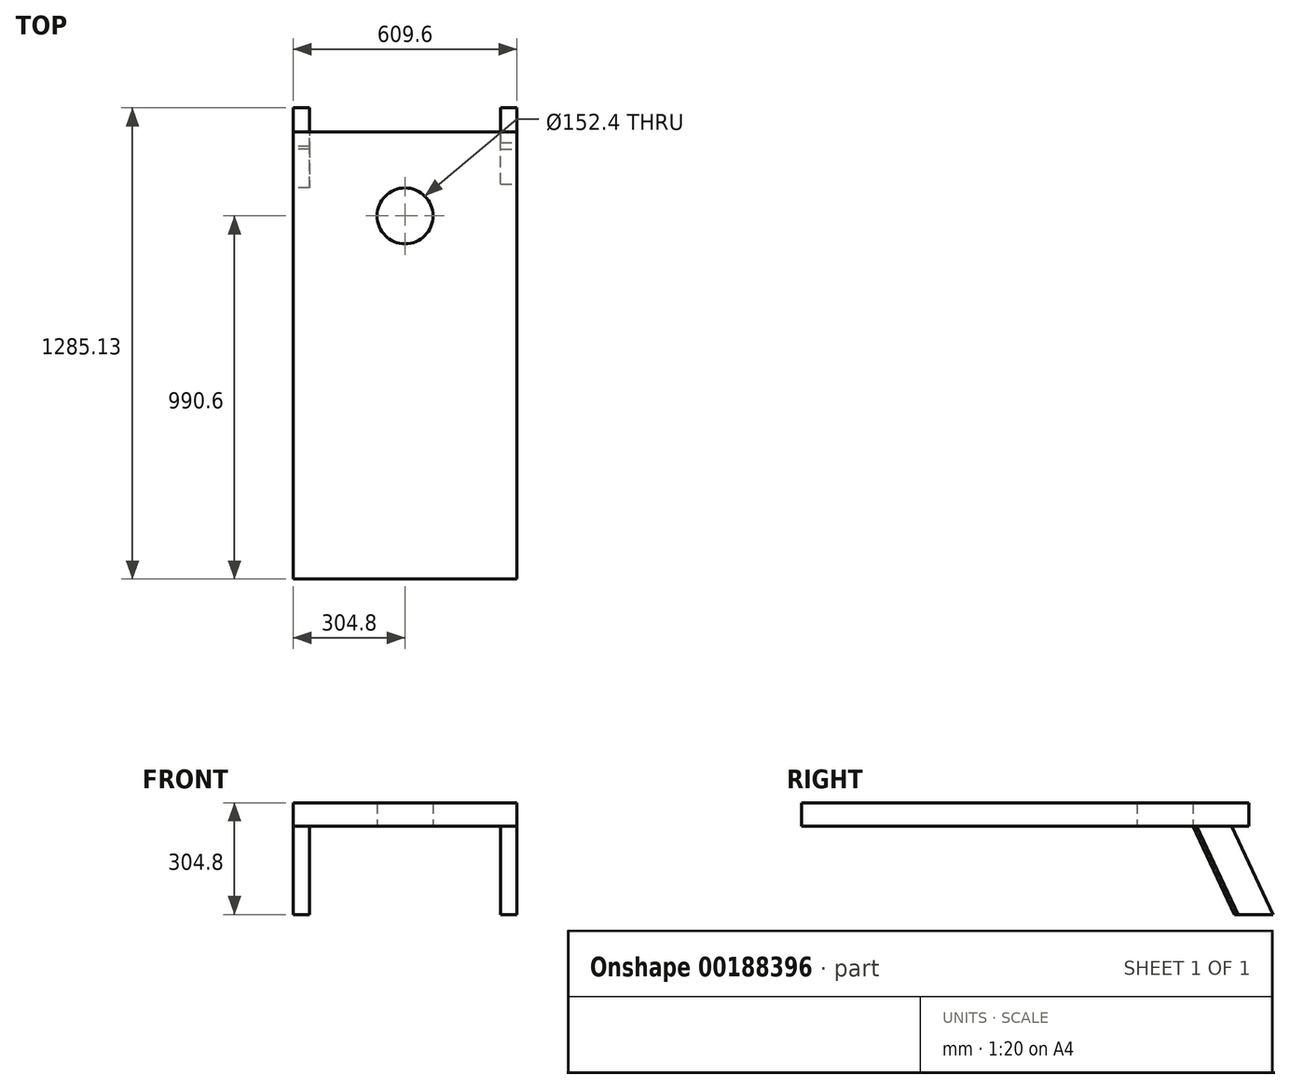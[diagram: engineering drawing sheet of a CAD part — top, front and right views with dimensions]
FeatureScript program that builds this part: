
annotation { "Feature Type Name" : "Feature", "Feature Type Description" : "" }
export const myFeature = defineFeature(function(context is Context, id is Id, definition is map)
    precondition{}
    {
        {
            var Q0;
            Q0=qCreatedBy(makeId("Top.planeOp"),FACE);
            var sketch = newSketch(context, id + "F0", { "sketchPlane" : qUnion([Q0])});
            skLineSegment(sketch, "E0.bottom", {"start": v(0, 0) * mm, "end": v(609.6, 0) * mm});
            skLineSegment(sketch, "E0.top", {"start": v(0, 1219.2) * mm, "end": v(609.6, 1219.2) * mm});
            skLineSegment(sketch, "E0.left", {"start": v(0, 0) * mm, "end": v(0, 1219.2) * mm});
            skLineSegment(sketch, "E0.right", {"start": v(609.6, 0) * mm, "end": v(609.6, 1219.2) * mm});
            skCircle(sketch, "E1", {"center": v(304.8, 990.6) * mm, "radius": 76.2 * mm});
            skLineSegment(sketch, "E2", {"start": v(0, 990.6) * mm, "end": v(609.6, 990.6) * mm});
            skLineSegment(sketch, "E3", {"start": v(304.8, 1219.2) * mm, "end": v(304.8, 0) * mm});
            skSolve(sketch);
        }
        {
            var Q0;
            {var subQ1=sQuery(id+"F0.wireOp",EDGE,"E0.left");var subQ5=sQuery(id+"F0.wireOp",EDGE,"E0.top");var subQ6=makeQuery(id+"F0.imprint","INTERSECT",VERTEX,{"derivedFrom":[subQ5,subQ1]});Q0=makeQuery(id+"F0.imprint","IMPRINT",FACE,{"disambiguationData":[TD([[makeQuery(id+"F0.imprint","IMPRINT",EDGE,{"disambiguationData":[TD([[subQ6,-1.0]])],"derivedFrom":subQ5}),-1.0]])]});}
            var Q1;
            {var subQ1=sQuery(id+"F0.wireOp",EDGE,"E0.right");var subQ7=sQuery(id+"F0.wireOp",EDGE,"E0.top");var subQ8=makeQuery(id+"F0.imprint","INTERSECT",VERTEX,{"derivedFrom":[subQ7,subQ1]});Q1=makeQuery(id+"F0.imprint","IMPRINT",FACE,{"disambiguationData":[TD([[makeQuery(id+"F0.imprint","IMPRINT",EDGE,{"disambiguationData":[TD([[subQ8,1.0]])],"derivedFrom":subQ7}),-1.0]])]});}
            var Q2;
            {var subQ1=sQuery(id+"F0.wireOp",EDGE,"E0.right");var subQ7=sQuery(id+"F0.wireOp",EDGE,"E0.bottom");var subQ8=makeQuery(id+"F0.imprint","INTERSECT",VERTEX,{"derivedFrom":[subQ7,subQ1]});Q2=makeQuery(id+"F0.imprint","IMPRINT",FACE,{"disambiguationData":[TD([[makeQuery(id+"F0.imprint","IMPRINT",EDGE,{"disambiguationData":[TD([[subQ8,1.0]])],"derivedFrom":subQ7}),1.0]])]});}
            var Q3;
            {var subQ1=sQuery(id+"F0.wireOp",EDGE,"E0.left");var subQ7=sQuery(id+"F0.wireOp",EDGE,"E0.bottom");var subQ8=makeQuery(id+"F0.imprint","INTERSECT",VERTEX,{"derivedFrom":[subQ7,subQ1]});Q3=makeQuery(id+"F0.imprint","IMPRINT",FACE,{"disambiguationData":[TD([[makeQuery(id+"F0.imprint","IMPRINT",EDGE,{"disambiguationData":[TD([[subQ8,-1.0]])],"derivedFrom":subQ7}),1.0]])]});}
            extrude(context, id + "F1", {"entities" : qUnion([Q0, Q1, Q2, Q3]), "depth" : 63.5 * mm});
        }
        {
            var Q0;
            Q0=makeQuery(id+"F1.opExtrude","SWEPT_FACE",FACE,{"disambiguationData":[OSD([sQuery(id+"F0.wireOp",EDGE,"E0.left")])]});
            var sketch = newSketch(context, id + "F2", { "sketchPlane" : qUnion([Q0])});
            skLineSegment(sketch, "E4", {"start": v(-1143, 63.5) * mm, "end": v(-1285.13, -241.3) * mm});
            skLineSegment(sketch, "E5", {"start": v(-1285.13, -241.3) * mm, "end": v(-1180.03, -241.3) * mm});
            skLineSegment(sketch, "E6", {"start": v(-1180.03, -241.3) * mm, "end": v(-1037.9, 63.5) * mm});
            skSolve(sketch);
        }
        {
            var Q0;
            {var subQ7=sQuery(id+"F2.wireOp",EDGE,"E5");Q0=makeQuery(id+"F2.imprint","IMPRINT",FACE,{"disambiguationData":[TD([[makeQuery(id+"F2.imprint","IMPRINT",EDGE,{"derivedFrom":subQ7}),1.0]])]});}
            extrude(context, id + "F3", {"entities" : qUnion([Q0]), "oppositeDirection" : true, "depth" : 44.45 * mm});
        }
        {
            var Q0;
            Q0=makeQuery(id+"F1.opExtrude","SWEPT_FACE",FACE,{"disambiguationData":[OSD([sQuery(id+"F0.wireOp",EDGE,"E0.right")])]});
            var sketch = newSketch(context, id + "F4", { "sketchPlane" : qUnion([Q0])});
            skLineSegment(sketch, "E7", {"start": v(1047.75, 63.5) * mm, "end": v(1189.88, -241.3) * mm});
            skLineSegment(sketch, "E8", {"start": v(1189.88, -241.3) * mm, "end": v(1285.13, -241.3) * mm});
            skLineSegment(sketch, "E9", {"start": v(1285.13, -241.3) * mm, "end": v(1143, 63.5) * mm});
            skSolve(sketch);
        }
        {
            var Q0;
            {var subQ0=sQuery(id+"F4.wireOp",EDGE,"E8");Q0=makeQuery(id+"F4.imprint","IMPRINT",FACE,{"disambiguationData":[TD([[makeQuery(id+"F4.imprint","IMPRINT",EDGE,{"derivedFrom":subQ0}),1.0]])]});}
            extrude(context, id + "F5", {"entities" : qUnion([Q0]), "oppositeDirection" : true, "depth" : 44.45 * mm});
        }
    });
